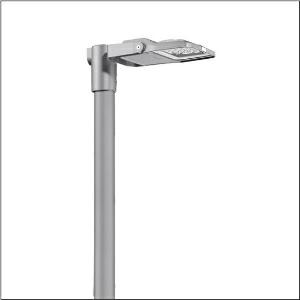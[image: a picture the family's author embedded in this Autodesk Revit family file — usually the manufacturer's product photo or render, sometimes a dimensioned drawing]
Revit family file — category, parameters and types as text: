
# Revit family: floodlight_fl_21_iq_micro___pl64_5xa7762a4e3a_dfd9
name_source: partatom
category: Lighting Fixtures
units: mm (PartAtom-declared; Revit-internal decimal feet)

## family parameters
Cut with Voids When Loaded = No
Host = Face
Light Source = No
Part Type = Normal
Room Calculation Point = No
Round Connector Dimension = Use Diameter
Shared = No

## types (1)
- --- (1 x LED, 2980 lm, 23.1 W, 4000K)
    Apparent Load = 23 VA
    CIE Flux Codes = 28 80 98 100 100
    Color Rendering = 70
    Color Temperature = 4000K
    Default Elevation = 1800 mm
    Description = Floodlight FL 21 iQ micro, floodlight, primary light control with lens, of PMMA, primary optical cover: protective disc, of toughened safety glass, transparent, light distribution: PL64, light emission: direct distribution, installation type: surface-mounted, LED, High Power LED, rated luminous flux: 2.980lm, luminous efficacy: 129lm/W, light colour: 740, colour temperature: 4000K, control: Auto-Match, Temp-Guard, Night-Set, Smart-Wire, Desk-Remote (wireless, voltage-free reading and setting of iQ features in the workshop via application-optimized NFC function/RFID function), optimised constant luminous flux control (CLO 2.0), Street-Remote, with terminal, 6-pole, mains connection: 220..240V, AC, 50/60Hz, start of lifetime: 23W, end of service life: 24W, reduction: 11W, luminaire housing, of diecast aluminium, powder-coated, Siteco® metallic grey (DB 702S), corrosivity category C5 mid according to DIN EN ISO 12944, sealing non-destructively replaceable, please order mast flange separately, mast bracket, of steel, galvanised, powder-coated, Siteco® metallic grey (DB 702S), protection rating (complete): IP66, insulation class (complete): insulation class II (safety insulation), certification: CE, ENEC, VDE, protection symbol: D, impact resistance: IK07, permissible operating ambient temperature: -40..+40°C, permissible operating ambient temperature for outdoor applications: -40..+50°C, standard: DIN EN 12944, LABS conformity tested according to VDMA 24364:2018-05, packaging unit: 1 piece

Light Distribution: PL64
    Height = 65 mm
    Lamp = 1 x LED
    Lamp Light Flux = 2980 lm
    Lamp Power = 23.1 W
    Lamp count = 1
    Length = 312 mm
    Luminous efficacy = 129 lm/W
    Manufacturer = Siteco
    ModVariant = No
    Model = 5XA7762A4E3A
    Number of Poles = 1
    OnlyDefault = Yes
    Power Factor = 1
    Product Name = Floodlight FL 21 iQ micro | PL64
    Product group = floodlight | pylon annexe
    ProductGroupID = 6200
    Protection Class = Protection class II
    Protection Degree = IP 66
    RLX_Detail_Level = 1
    RLX_Emergency_Light_Flux = 0 lm
    RLX_Emergency_Type = 0
    RLX_Emergency_Type_DB = No
    RlxData = <blob elided: 101593 chars, md5=a27778b8>
    Socket = socket
    Standby Power = 0 W
    System Light Flux = 2980 lm
    System Power = 23 W
    Type Comments = factory setting: luminous flux: 100 % | dim-lin: 254 | 455 mA
    Type Image = l_1007121.jpg
    URL = http://relux.com
    VarID = @adj_131907
    Voltage = 0 V
    Weight = 0.00 kg
    Width = 230 mm

## geometry (parser evidence)
native form markers: Blend x4, Sweep x11
no freeform markers — native parametric forms only
